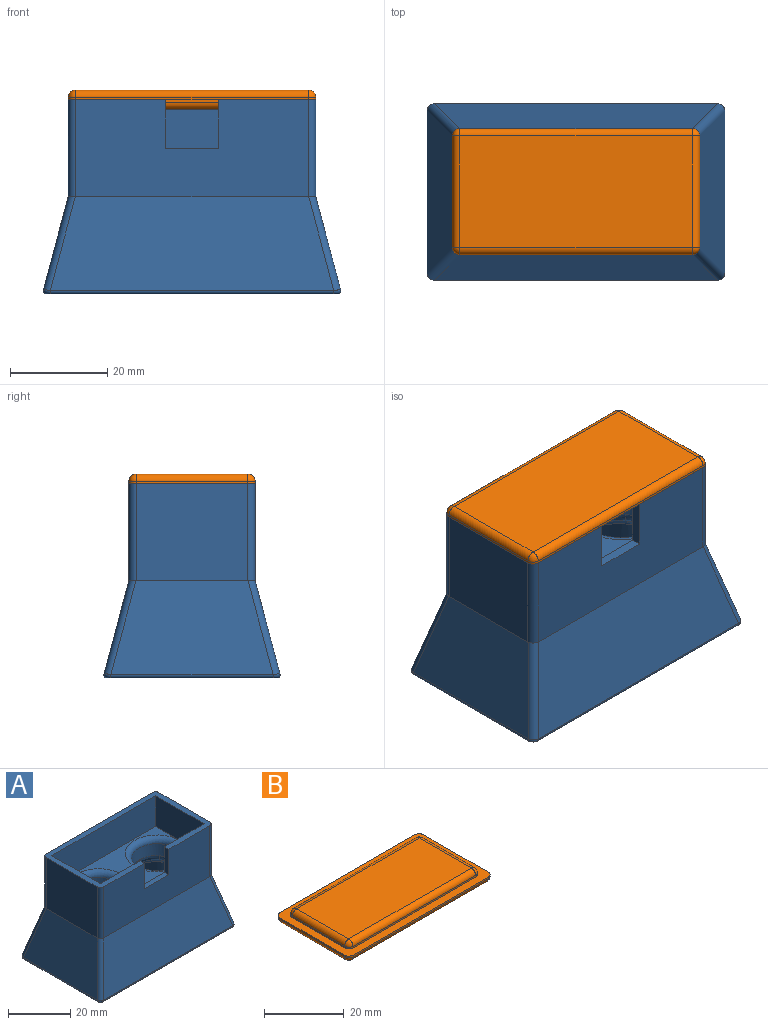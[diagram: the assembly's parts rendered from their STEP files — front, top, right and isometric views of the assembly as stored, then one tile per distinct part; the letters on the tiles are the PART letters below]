
ASSEMBLY  parts=2 mates=1
PART A: 98 faces, bbox 61.4x36.4x40 mm
  f0: plane 16.49x10.89mm, normal (0,0,-1), area 98.8mm2, adj f55,f68,f72,f84
  f1: plane 12.27x12.27mm, normal (0,0,-1), area 31.4mm2, adj f32,f33,f35,f47
  f2: plane 12.27x12.27mm, normal (0,0,-1), area 31.4mm2, adj f35,f37,f38,f45
  f3: plane 12.27x12.27mm, normal (0,0,-1), area 31.4mm2, adj f32,f34,f36,f43
  f4: plane 12.27x12.27mm, normal (0,0,-1), area 31.4mm2, adj f36,f38,f39,f41
  f5: plane 51x26mm, normal (0,0,1), area 268.1mm2, adj f6,f16,f17,f18,f21,f22,f23,f24
  f6: plane 48x20mm, normal (0,-1,0), area 850mm2, adj f5,f11,f25,f26,f27,f50,f51
  f7: plane 47x22mm, normal (0,0,1), area 373.9mm2, adj f21,f22,f23,f24,f96,f97
  f8: plane 33.42x19.25mm, normal (0.97,0,0.26), area 563mm2, adj f16,f35,f44,f46,f48,f51
  f9: plane 58.42x19.25mm, normal (0,0.97,0.26), area 1061.1mm2, adj f17,f38,f40,f44,f48,f49
  f10: plane 33.42x19.25mm, normal (-0.97,0,0.26), area 563mm2, adj f18,f36,f40,f42,f49,f50
  f11: plane 58.42x19.25mm, normal (0,-0.97,0.26), area 1061.1mm2, adj f6,f32,f42,f46,f50,f51
  f12: plane 14.71x10.62mm, normal (-0.97,0,-0.26), area 101.7mm2, adj f29,f31,f35,f65
  f13: plane 35.62x14.65mm, normal (0,-0.97,-0.26), area 480.7mm2, adj f30,f31,f38,f64,f66,f68,f70,f71
  f14: plane 14.71x10.62mm, normal (0.97,0,-0.26), area 101.7mm2, adj f28,f30,f36,f58
  f15: plane 35.62x14.65mm, normal (0,0.97,-0.26), area 480.7mm2, adj f28,f29,f32,f52,f53,f55,f57,f59
  f16: plane 23x20mm, normal (1,0,0), area 460mm2, adj f5,f8,f48,f51
  f17: plane 48x20mm, normal (0,1,0), area 960mm2, adj f5,f9,f48,f49
  f18: plane 23x20mm, normal (-1,0,0), area 460mm2, adj f5,f10,f49,f50
  f19: cylinder r=8.25mm len=16.5mm, axis (0,0,1), area 234.4mm2, adj f84,f85,f86,f87,f88,f89,f90,f91
  f20: cylinder r=8.25mm len=16.5mm, axis (0,0,1), area 234.4mm2, adj f72,f73,f74,f75,f76,f77,f78,f79
  f21: plane 22x12mm, normal (-1,0,0), area 264mm2, adj f5,f7,f22,f24
  f22: plane 47x12mm, normal (0,1,0), area 454mm2, adj f5,f7,f21,f23,f25,f26,f27
  f23: plane 22x12mm, normal (1,0,0), area 264mm2, adj f5,f7,f22,f24
  f24: plane 47x12mm, normal (0,-1,0), area 564mm2, adj f5,f7,f21,f23
  f25: plane 10x2mm, normal (-1,0,0), area 20mm2, adj f5,f6,f22,f27
  f26: plane 10x2mm, normal (1,0,0), area 20mm2, adj f5,f6,f22,f27
  f27: plane 11x2mm, normal (0,0,1), area 22mm2, adj f6,f22,f25,f26
  f28: cylinder r=12.1mm len=15.85mm, axis (-0.25,-0.25,-0.94), area 278.9mm2, adj f14,f15,f34,f54,f56
  f29: cylinder r=12.1mm len=15.85mm, axis (0.25,-0.25,-0.94), area 278.9mm2, adj f12,f15,f33,f61,f63
  f30: cylinder r=12.1mm len=15.85mm, axis (-0.25,0.25,-0.94), area 278.9mm2, adj f13,f14,f39,f60,f62
  f31: cylinder r=12.1mm len=15.85mm, axis (0.25,0.25,-0.94), area 278.9mm2, adj f12,f13,f37,f67,f69
  f32: cylinder r=0.6mm len=58.42mm, axis (-1,0,0), area 92.2mm2, adj f1,f3,f11,f15,f33,f34,f43,f47
  f33: bspline ~12.27x12.27mm, area 14mm2, adj f1,f29,f32,f35
  f34: bspline ~12.27x12.27mm, area 14mm2, adj f3,f28,f32,f36
  f35: cylinder r=0.6mm len=33.42mm, axis (0,-1,0), area 45.1mm2, adj f1,f2,f8,f12,f33,f37,f45,f47
  f36: cylinder r=0.6mm len=33.42mm, axis (0,1,0), area 45.1mm2, adj f3,f4,f10,f14,f34,f39,f41,f43
  f37: bspline ~12.27x12.27mm, area 14mm2, adj f2,f31,f35,f38
  f38: cylinder r=0.6mm len=58.42mm, axis (1,0,0), area 92.2mm2, adj f2,f4,f9,f13,f37,f39,f41,f45
  f39: bspline ~12.27x12.27mm, area 14mm2, adj f4,f30,f36,f38
  f40: cylinder r=1.5mm len=19.39mm, axis (0.25,-0.25,0.94), area 46.4mm2, adj f9,f10,f41,f49
  f41: bspline ~1.47x1.47mm, area 2.3mm2, adj f4,f36,f38,f40
  f42: cylinder r=1.5mm len=19.39mm, axis (0.25,0.25,0.94), area 46.4mm2, adj f10,f11,f43,f50
  f43: bspline ~1.47x1.47mm, area 2.3mm2, adj f3,f32,f36,f42
  f44: cylinder r=1.5mm len=19.39mm, axis (-0.25,-0.25,0.94), area 46.4mm2, adj f8,f9,f45,f48
  f45: bspline ~1.47x1.47mm, area 2.3mm2, adj f2,f35,f38,f44
  f46: cylinder r=1.5mm len=19.39mm, axis (-0.25,0.25,0.94), area 46.4mm2, adj f8,f11,f47,f51
  f47: bspline ~1.47x1.47mm, area 2.3mm2, adj f1,f32,f35,f46
  f48: cylinder r=1.5mm len=20mm, axis (0,0,1), area 47mm2, adj f5,f8,f9,f16,f17,f44
  f49: cylinder r=1.5mm len=20mm, axis (0,0,-1), area 47mm2, adj f5,f9,f10,f17,f18,f40
  f50: cylinder r=1.5mm len=20mm, axis (0,0,1), area 47mm2, adj f5,f6,f10,f11,f18,f42
  f51: cylinder r=1.5mm len=20mm, axis (0,0,-1), area 47mm2, adj f5,f6,f8,f11,f16,f46
  f52: cylinder r=5mm len=3.33mm, axis (1,0,0), area 1.3mm2, adj f15,f53,f54,f78
  f53: bspline ~4.95x3.8mm, area 3.2mm2, adj f15,f52,f55,f76
  f54: bspline ~9.42x6.64mm, area 42.1mm2, adj f28,f52,f56,f80
  f55: cylinder r=5mm len=25.8mm, axis (1,0,0), area 154.2mm2, adj f0,f15,f53,f57,f74,f86
  f56: bspline ~8.85x6.79mm, area 26.5mm2, adj f28,f54,f58,f82
  f57: bspline ~4.95x3.8mm, area 3.2mm2, adj f15,f55,f59,f88
  f58: bspline ~7.19x5.24mm, area 11.5mm2, adj f14,f56,f60,f83
  f59: cylinder r=5mm len=3.33mm, axis (1,0,0), area 1.3mm2, adj f15,f57,f61,f90
  f60: bspline ~8.66x6.31mm, area 26.5mm2, adj f30,f58,f62,f81
  f61: bspline ~9.42x6.64mm, area 42.1mm2, adj f29,f59,f63,f92
  f62: bspline ~9.42x6.64mm, area 42.1mm2, adj f30,f60,f64,f79
  f63: bspline ~8.66x6.31mm, area 26.5mm2, adj f29,f61,f65,f94
  f64: cylinder r=5mm len=3.33mm, axis (1,0,0), area 1.3mm2, adj f13,f62,f66,f77
  f65: bspline ~7.19x5.24mm, area 11.5mm2, adj f12,f63,f67,f95
  f66: bspline ~4.95x3.8mm, area 3.2mm2, adj f13,f64,f68,f75
  f67: bspline ~8.85x6.79mm, area 26.5mm2, adj f31,f65,f69,f93
  f68: cylinder r=5mm len=25.8mm, axis (1,0,0), area 154.2mm2, adj f0,f13,f66,f70,f73,f85
  f69: bspline ~9.42x6.64mm, area 42.1mm2, adj f31,f67,f71,f91
  f70: bspline ~4.95x3.8mm, area 3.2mm2, adj f13,f68,f71,f87
  f71: cylinder r=5mm len=3.33mm, axis (1,0,0), area 1.3mm2, adj f13,f69,f70,f89
  f72: torus R=11.35mm, axis (0,0,1), area 74.2mm2, adj f0,f20,f73,f74
  f73: bspline ~9.02x5.14mm, area 27.2mm2, adj f20,f68,f72,f75
  f74: bspline ~10.05x5.14mm, area 27.2mm2, adj f20,f55,f72,f76
  f75: bspline ~2.92x2.83mm, area 2.2mm2, adj f20,f66,f73,f77
  f76: bspline ~2.92x2.83mm, area 2.2mm2, adj f20,f53,f74,f78
  f77: bspline ~2.92x2.77mm, area 0.9mm2, adj f20,f64,f75,f79
  f78: bspline ~2.89x1.97mm, area 0.9mm2, adj f20,f52,f76,f80
  f79: bspline ~9.08x5.74mm, area 27mm2, adj f20,f62,f77,f81
  f80: bspline ~8.62x5.75mm, area 27mm2, adj f20,f54,f78,f82
  f81: bspline ~7.28x4.17mm, area 17.2mm2, adj f20,f60,f79,f83
  f82: bspline ~7.28x4.17mm, area 17.2mm2, adj f20,f56,f80,f83
  f83: bspline ~4.93x2.86mm, area 8.4mm2, adj f20,f58,f81,f82
  f84: torus R=11.35mm, axis (0,0,1), area 74.2mm2, adj f0,f19,f85,f86
  f85: bspline ~10.05x5.14mm, area 27.2mm2, adj f19,f68,f84,f87
  f86: bspline ~9.02x5.14mm, area 27.2mm2, adj f19,f55,f84,f88
  f87: bspline ~2.92x2.83mm, area 2.2mm2, adj f19,f70,f85,f89
  f88: bspline ~2.92x2.83mm, area 2.2mm2, adj f19,f57,f86,f90
  f89: bspline ~2.89x1.97mm, area 0.9mm2, adj f19,f71,f87,f91
  f90: bspline ~2.92x2.77mm, area 0.9mm2, adj f19,f59,f88,f92
  f91: bspline ~8.85x5.75mm, area 27mm2, adj f19,f69,f89,f93
  f92: bspline ~9.08x5.74mm, area 27mm2, adj f19,f61,f90,f94
  f93: bspline ~7.28x4.17mm, area 17.2mm2, adj f19,f67,f91,f95
  f94: bspline ~7.28x4.17mm, area 17.2mm2, adj f19,f63,f92,f95
  f95: bspline ~4.93x2.86mm, area 8.4mm2, adj f19,f65,f93,f94
  f96: torus R=10.25mm, axis (0,0,1), area 177.2mm2, adj f7,f19
  f97: torus R=10.25mm, axis (0,0,1), area 177.2mm2, adj f7,f20
PART B: 35 faces, bbox 51x26x4 mm
  f0: plane 23x0.5mm, normal (1,0,0), area 11.5mm2, adj f4,f16,f20,f22
  f1: plane 48x0.5mm, normal (0,1,0), area 24mm2, adj f4,f13,f19,f22
  f2: plane 23x0.5mm, normal (-1,0,0), area 11.5mm2, adj f4,f11,f13,f14
  f3: plane 48x0.5mm, normal (0,-1,0), area 24mm2, adj f4,f11,f15,f16
  f4: plane 51x26mm, normal (0,0,1), area 326.3mm2, adj f0,f1,f2,f3,f7,f8,f9,f10
  f5: plane 48x23mm, normal (0,0,-1), area 1104mm2, adj f14,f15,f19,f20
  f6: plane 43.5x18.5mm, normal (0,0,1), area 804.7mm2, adj f26,f27,f31,f32
  f7: plane 18.5x0.5mm, normal (-1,0,0), area 9.2mm2, adj f4,f23,f27,f28
  f8: plane 43.5x0.5mm, normal (0,-1,0), area 21.8mm2, adj f4,f23,f25,f26
  f9: plane 18.5x0.5mm, normal (1,0,0), area 9.2mm2, adj f4,f25,f31,f34
  f10: plane 43.5x0.5mm, normal (0,1,0), area 21.8mm2, adj f4,f28,f32,f34
  f11: cylinder r=1.5mm len=1.5mm, axis (0,0,1), area 1.2mm2, adj f2,f3,f4,f12
  f12: sphere r=1.5mm, area 3.5mm2, adj f11,f14,f15
  f13: cylinder r=1.5mm len=1.5mm, axis (0,0,-1), area 1.2mm2, adj f1,f2,f4,f17
  f14: cylinder r=1.5mm len=23mm, axis (0,-1,0), area 54.2mm2, adj f2,f5,f12,f17
  f15: cylinder r=1.5mm len=48mm, axis (1,0,0), area 113.1mm2, adj f3,f5,f12,f18
  f16: cylinder r=1.5mm len=1.5mm, axis (0,0,-1), area 1.2mm2, adj f0,f3,f4,f18
  f17: sphere r=1.5mm, area 3.5mm2, adj f13,f14,f19
  f18: sphere r=1.5mm, area 3.5mm2, adj f15,f16,f20
  f19: cylinder r=1.5mm len=48mm, axis (-1,0,0), area 113.1mm2, adj f1,f5,f17,f21
  f20: cylinder r=1.5mm len=23mm, axis (0,1,0), area 54.2mm2, adj f0,f5,f18,f21
  f21: sphere r=1.5mm, area 3.5mm2, adj f19,f20,f22
  f22: cylinder r=1.5mm len=1.5mm, axis (0,0,1), area 1.2mm2, adj f0,f1,f4,f21
  f23: cylinder r=1.5mm len=1.5mm, axis (0,0,1), area 1.2mm2, adj f4,f7,f8,f24
  f24: sphere r=1.5mm, area 3.5mm2, adj f23,f26,f27
  f25: cylinder r=1.5mm len=1.5mm, axis (0,0,-1), area 1.2mm2, adj f4,f8,f9,f29
  f26: cylinder r=1.5mm len=43.5mm, axis (-1,0,0), area 102.5mm2, adj f6,f8,f24,f29
  f27: cylinder r=1.5mm len=18.5mm, axis (0,1,0), area 43.6mm2, adj f6,f7,f24,f30
  f28: cylinder r=1.5mm len=1.5mm, axis (0,0,-1), area 1.2mm2, adj f4,f7,f10,f30
  f29: sphere r=1.5mm, area 3.5mm2, adj f25,f26,f31
  f30: sphere r=1.5mm, area 3.5mm2, adj f27,f28,f32
  f31: cylinder r=1.5mm len=18.5mm, axis (0,-1,0), area 43.6mm2, adj f6,f9,f29,f33
  f32: cylinder r=1.5mm len=43.5mm, axis (1,0,0), area 102.5mm2, adj f6,f10,f30,f33
  f33: sphere r=1.5mm, area 3.5mm2, adj f31,f32,f34
  f34: cylinder r=1.5mm len=1.5mm, axis (0,0,1), area 1.2mm2, adj f4,f9,f10,f33
PLACE A t=(-16.39,-9.52,-3.09)mm
PLACE B rot(axis=(1,0,0),180deg) t=(-16.39,-9.52,18.91)mm
MATE planar B.f4 <-> A.f5  axis (0,0,-1) through (-16.39,3.48,16.91)mm
